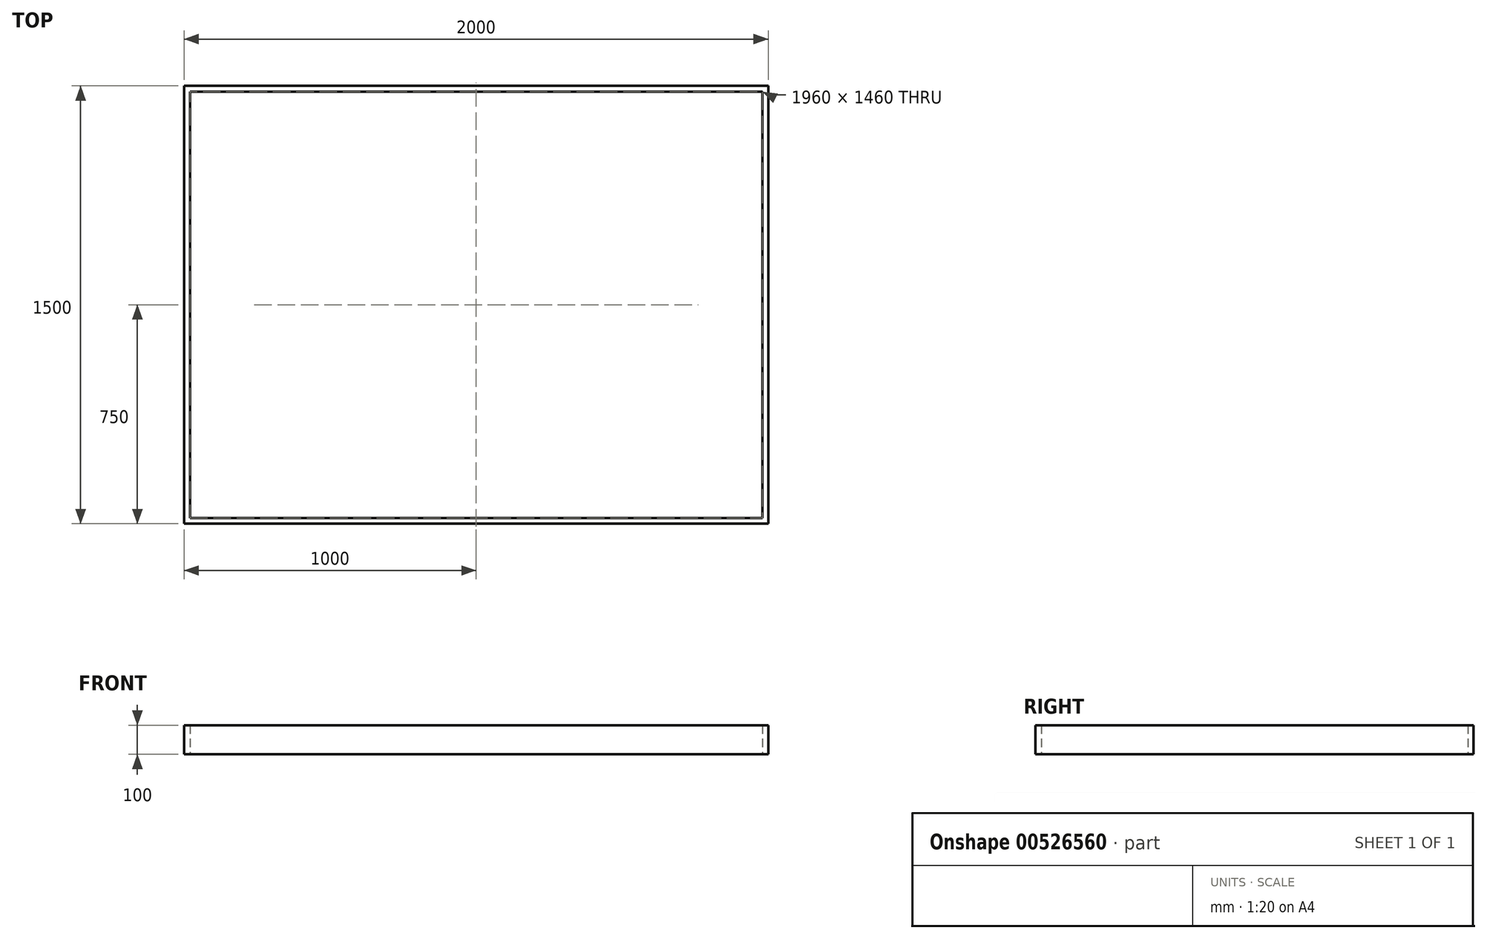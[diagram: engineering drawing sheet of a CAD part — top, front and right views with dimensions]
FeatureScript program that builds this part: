
annotation { "Feature Type Name" : "Feature", "Feature Type Description" : "" }
export const myFeature = defineFeature(function(context is Context, id is Id, definition is map)
    precondition{}
    {
        {
            var Q0;
            Q0=qCreatedBy(makeId("Top.planeOp"),FACE);
            var sketch = newSketch(context, id + "F0", { "sketchPlane" : qUnion([Q0])});
            skLineSegment(sketch, "E0.bottom", {"start": v(0, 0) * mm, "end": v(2000, 0) * mm});
            skLineSegment(sketch, "E0.top", {"start": v(0, -1500) * mm, "end": v(2000, -1500) * mm});
            skLineSegment(sketch, "E0.left", {"start": v(0, 0) * mm, "end": v(0, -1500) * mm});
            skLineSegment(sketch, "E0.right", {"start": v(2000, 0) * mm, "end": v(2000, -1500) * mm});
            skLineSegment(sketch, "E1.bottom", {"start": v(20, -20) * mm, "end": v(1980, -20) * mm});
            skLineSegment(sketch, "E1.top", {"start": v(20, -1480) * mm, "end": v(1980, -1480) * mm});
            skLineSegment(sketch, "E1.left", {"start": v(20, -20) * mm, "end": v(20, -1480) * mm});
            skLineSegment(sketch, "E1.right", {"start": v(1980, -20) * mm, "end": v(1980, -1480) * mm});
            skSolve(sketch);
        }
        {
            var Q0;
            Q0 = qSketchRegion(id + "F0", true);
            extrude(context, id + "F1", {"entities" : qUnion([Q0]), "depth" : 100 * mm, "offsetDistance" : 25 * mm});
        }
    });
